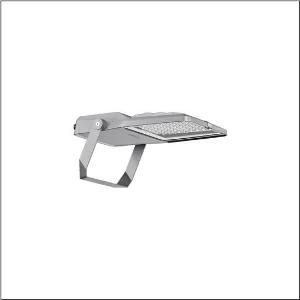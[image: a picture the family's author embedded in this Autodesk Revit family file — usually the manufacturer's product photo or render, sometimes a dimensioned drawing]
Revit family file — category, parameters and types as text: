
# Revit family: floodlight_fl_21_iq_mini___pl33t_5xa7772b3f1a_8999
name_source: partatom
category: Lighting Fixtures
units: mm (PartAtom-declared; Revit-internal decimal feet)

## family parameters
Cut with Voids When Loaded = No
Host = Face
Light Source = No
Part Type = Normal
Room Calculation Point = No
Round Connector Dimension = Use Diameter
Shared = No

## types (1)
- --- (1 x LED, 5310 lm, 45.5 W, 3000K)
    Apparent Load = 46 VA
    CIE Flux Codes = 26 75 99 100 100
    Color Rendering = 80
    Color Temperature = 3000K
    Default Elevation = 1800 mm
    Description = Floodlight FL 21 iQ mini, floodlight, primary light control with lens, of PMMA, primary optical cover: protective disc, of toughened safety glass, transparent, light distribution: PL33T, light emission: direct distribution, installation type: surface-mounted, LED, High Power LED, rated luminous flux: 5.310lm, luminous efficacy: 117lm/W, light colour: 830, colour temperature: 3000K, control: Street-Remote, Auto-Match, Temp-Guard, Night-Set, Smart-Wire, Desk-Remote (wireless, voltage-free reading and setting of iQ features in the workshop via application-optimized NFC function/RFID function), optimised constant luminous flux control (CLO 2.0), with terminal, 6-pole, mains connection: 220..240V, AC, 50/60Hz, start of lifetime: 46W, end of service life: 48W, reduction: 21W, luminaire housing, of diecast aluminium, powder-coated, Siteco® metallic grey (DB 702S), corrosivity category C5 mid according to DIN EN ISO 12944, sealing non-destructively replaceable, mounting bracket, of steel, galvanised, powder-coated, Siteco® metallic grey (DB 702S), protection rating (complete): IP66, insulation class (complete): insulation class II (safety insulation), certification: CE, ENEC, VDE, protection symbol: D, impact resistance: IK08, permissible operating ambient temperature: -40..+40°C, permissible operating ambient temperature for outdoor applications: -40..+50°C, standard: DIN EN 12944, LABS conformity tested according to VDMA 24364:2018-05, packaging unit: 1 piece

Light Distribution: PL33T
    Height = 70 mm
    Lamp = 1 x LED
    Lamp Light Flux = 5310 lm
    Lamp Power = 45.5 W
    Lamp count = 1
    Length = 485 mm
    Luminous efficacy = 117 lm/W
    Manufacturer = Siteco
    ModVariant = No
    Model = 5XA7772B3F1A
    Number of Poles = 1
    OnlyDefault = Yes
    Power Factor = 1
    Product Name = Floodlight FL 21 iQ mini | PL33T
    Product group = floodlight | pylon annexe
    ProductGroupID = 6200
    Protection Class = Protection class II
    Protection Degree = IP 66
    RLX_Detail_Level = 1
    RLX_Emergency_Light_Flux = 0 lm
    RLX_Emergency_Type = 0
    RLX_Emergency_Type_DB = No
    RlxData = <blob elided: 96013 chars, md5=b8d41d0b>
    Socket = socket
    Standby Power = 0 W
    System Light Flux = 5310 lm
    System Power = 46 W
    Type Comments = factory setting: luminous flux: 100 % | dim-lin: 254 | 463 mA
    Type Image = l_1006845.jpg
    URL = http://relux.com
    VarID = @adj_082479
    Voltage = 0 V
    Weight = 0.00 kg
    Width = 337 mm

## geometry (parser evidence)
native form markers: Blend x4, Sweep x13
no freeform markers — native parametric forms only
